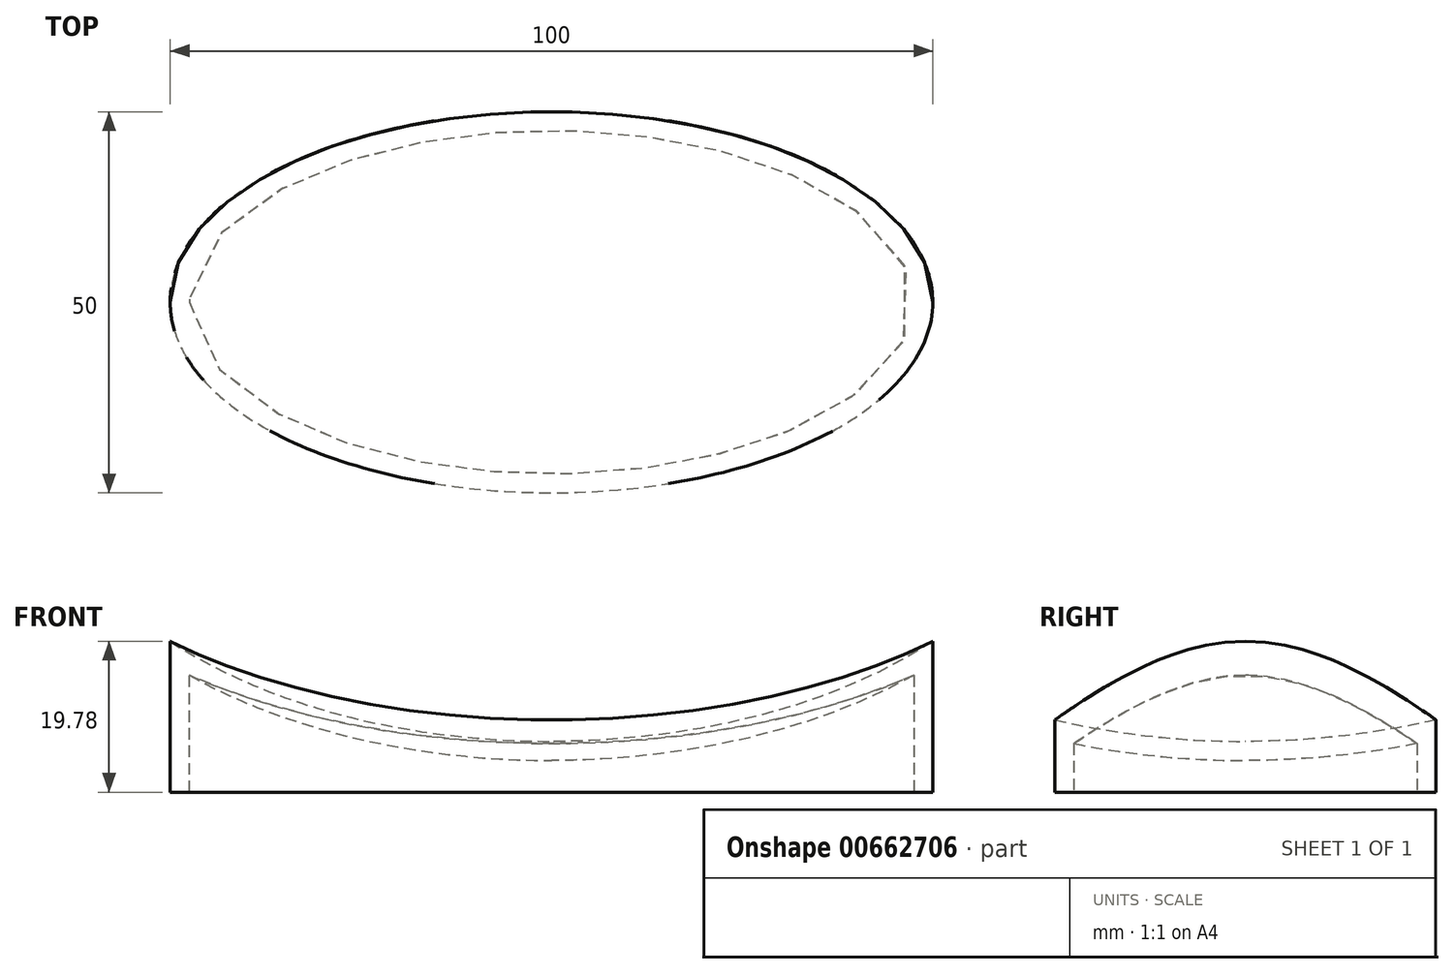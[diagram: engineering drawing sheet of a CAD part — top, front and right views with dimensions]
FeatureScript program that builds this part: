
annotation { "Feature Type Name" : "Feature", "Feature Type Description" : "" }
export const myFeature = defineFeature(function(context is Context, id is Id, definition is map)
    precondition{}
    {
        {
            var Q0;
            Q0=qCreatedBy(makeId("Top.planeOp"),FACE);
            var sketch = newSketch(context, id + "F0", { "sketchPlane" : qUnion([Q0])});
            skEllipse(sketch, "E0", {"center": v(0, 0) * mm, "majorRadius": 50 * mm, "minorRadius": 25 * mm, "majorAxis": v(1, 0)});
            skSolve(sketch);
        }
        {
            var Q0;
            Q0=makeQuery(id+"F0.imprint","IMPRINT",FACE,{"disambiguationData":[TD([[makeQuery(id+"F0.imprint","IMPRINT",EDGE,{"derivedFrom":sQuery(id+"F0.wireOp",EDGE,"E0")}),1.0]])]});
            extrude(context, id + "F1", {"entities" : qUnion([Q0]), "depth" : 20 * mm, "offsetDistance" : 25 * mm});
        }
        {
            var Q0;
            Q0=qCreatedBy(makeId("Front.planeOp"),FACE);
            var sketch = newSketch(context, id + "F2", { "sketchPlane" : qUnion([Q0])});
            skEllipticalArc(sketch, "E1", {});
            skLineSegment(sketch, "E2", {"start": v(0, 6.65) * mm, "end": v(0, 30.82) * mm});
            skLineSegment(sketch, "E3", {"start": v(0, 30.82) * mm, "end": v(-66.34, 50.2) * mm});
            const initialGuessF2  = {"E1": [0, 0.04561508819460869, 0, -1, 0.038963479455560446, 0.06679959649421735, 4.594415937341404, 6.283185307179586]};
            skSetInitialGuess(sketch, initialGuessF2);
            skSolve(sketch);
        }
        {
            var Q0;
            Q0=qCreatedBy(makeId("Front.planeOp"),FACE);
            var sketch = newSketch(context, id + "F3", { "sketchPlane" : qUnion([Q0])});
            skLineSegment(sketch, "E4", {"start": v(0, 64.03) * mm, "end": v(0, -21.2) * mm, "construction": true});
            skSolve(sketch);
        }
        {
            var Q0;
            Q0=makeQuery(id+"F2.imprint","IMPRINT",FACE,{"disambiguationData":[TD([[makeQuery(id+"F2.imprint","IMPRINT",EDGE,{"derivedFrom":sQuery(id+"F2.wireOp",EDGE,"E1")}),1.0]])]});
            var Q1;
            Q1=sQuery(id+"F3.wireOp",EDGE,"E4");
            revolve(context, id + "F4", {"operationType" : NewBodyOperationType.REMOVE, "entities" : qUnion([Q0]), "axis" : qUnion([Q1]), "revolveType" : RevolveType.FULL, "oppositeDirection" : true});
        }
        {
            var Q0;
            Q0=makeQuery(id+"F1.opExtrude","CAP_FACE",FACE,{"disambiguationData":[OSD([sQuery(id+"F0.wireOp",EDGE,"E0")])],"isStart":true});
            shell(context, id + "F5", {"entities" : qUnion([Q0]), "thickness" : 2.5 * mm});
        }
    });
